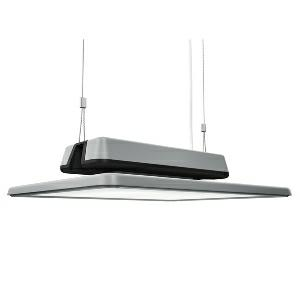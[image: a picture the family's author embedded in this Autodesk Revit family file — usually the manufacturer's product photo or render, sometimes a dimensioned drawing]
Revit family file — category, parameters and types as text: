
# Revit family: acaneo_-_hial_30000_840_w_ea_00734136_9b87
name_source: partatom
category: Lighting Fixtures
units: mm (PartAtom-declared; Revit-internal decimal feet)

## family parameters
Cut with Voids When Loaded = No
Host = Face
Light Source = No
Part Type = Normal
Room Calculation Point = No
Round Connector Dimension = Use Diameter
Shared = No

## types (1)
- ACANEO - HIAL 30000/840/W/EA (1 x LED, 33000 lm, 4000K)
    Apparent Load = 206 VA
    Approval mark = CE
    CIE Flux Codes = 76 97 99 100 100
    Color Rendering = 80-89
    Color Temperature = 4000K
    Control Gear = Electronic ballast
    Default Elevation = 1800 mm
    Description = HIAL 30000/840/W/EA|High bay luminaire|light source: LED|work equipment: Electronic ballast|connected load: 220-240 V, 50/60 Hz|Power consumption: approx. 206 W|power factor: approx. 0,973|luminous flux: 33000 lm|luminous efficacy: 160 lm/W|colour temperature: Cold white, ca. 4000 K|color rendering index (CRI): >= 80|chromaticity tolerance:  3 SDCM|System of protection: IP 65|class of protection: I|technology: Switchable|luminaire body|material: Aluminium|surface: Powder coatet|colour: White aluminium|lamp cover: Acrylic (PMMA), Clear|weight (net): approx. 10.8 kg|mains lead: Built-in plug RST 25i3 Einbau|Fastening: Available separately|Accessory: Junction box (RST 2013)|minimum ambient temperature: -30 ░C|maximum ambient temperature: 50 ░C|glare control: Optics|unified glare rating(4H 8H): <=  25|
    Frequency = 50 Hz, 60 Hz
    Height = 125 mm
    Lamp = 1 x LED
    Lamp Light Flux = 33000 lm
    Lamp count = 1
    Length = 585 mm
    Luminous efficacy = 160 lm/W
    Manufacturer = Waldmann
    ModVariant = No
    Model = 00734136
    Mounting Place = Ceiling
    Mounting Type = Pendant
    Number of Poles = 1
    OnlyDefault = Yes
    Power Factor = 1
    Product Name = ACANEO - HIAL 30000/840/W/EA
    Product group = High bay luminaire (industry)
    ProductGroupID = 901
    Protection Class = Protection class I
    Protection Degree = IP 65
    RLX_Detail_Level = 1
    RLX_Emergency_Light_Flux = 0 lm
    RLX_Emergency_Type = 0
    RLX_Emergency_Type_DB = No
    RlxData = <blob elided: 29897 chars, md5=de37d627>
    Socket = socket
    Standby Power = 0 W
    System Light Flux = 32999 lm
    System Power = 206 W
    Type Comments = Product without accessories
    Type Image = acaneo-hial.jpg
    URL = http://relux.com
    VarID = ---
    Voltage = 230 V
    Voltage Range = 110-120 V, 220-240 V
    Weight = 0.00 kg
    Width = 480 mm

## geometry (parser evidence)
native form markers: Blend x4, Sweep x8
no freeform markers — native parametric forms only
